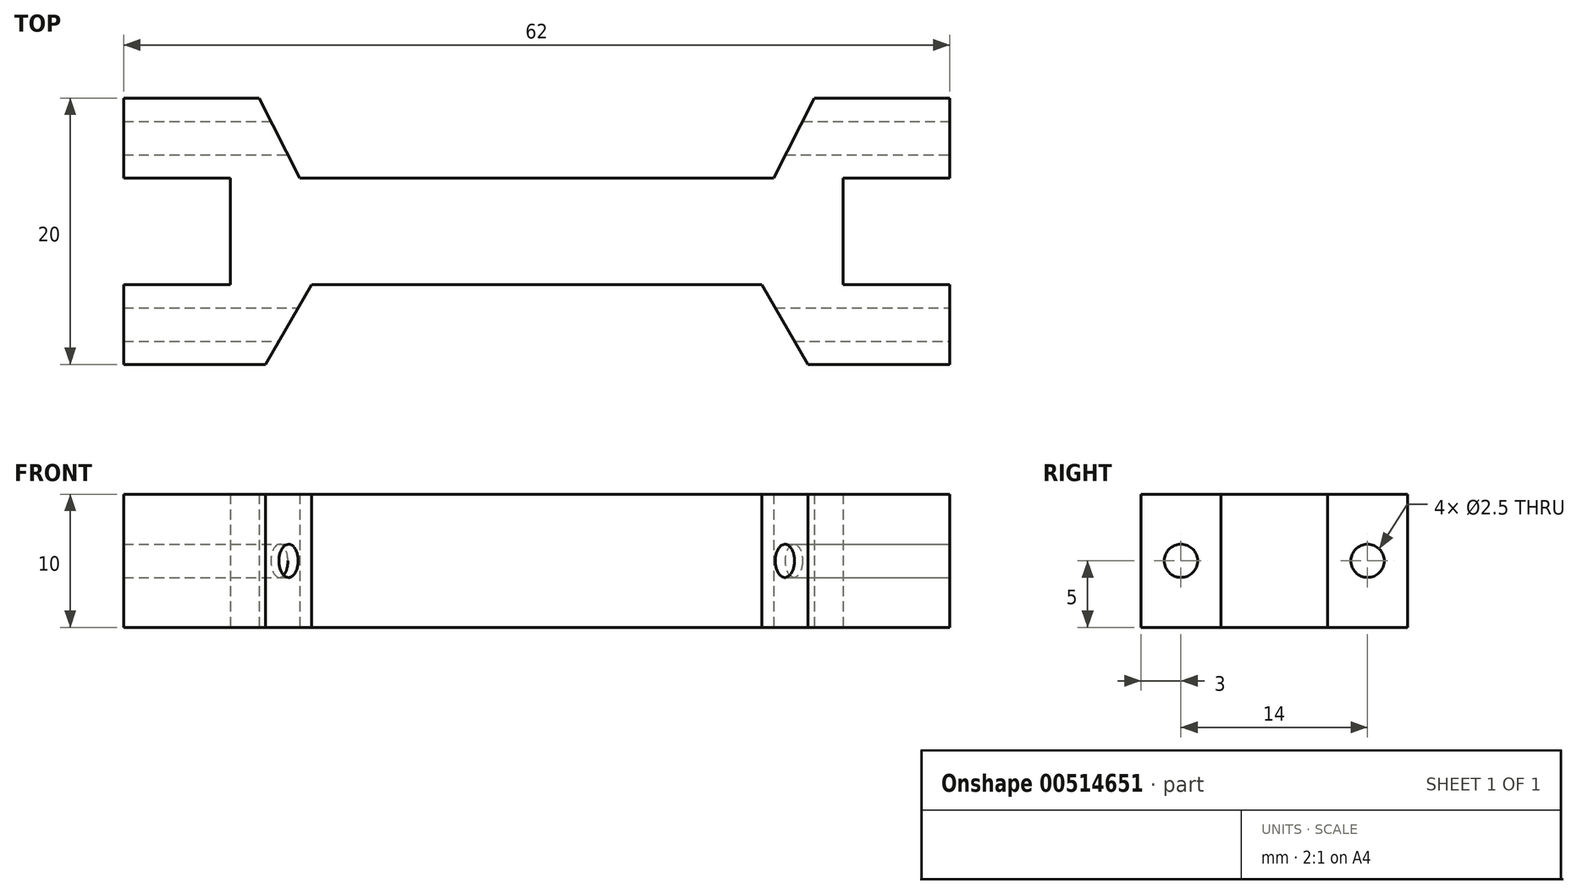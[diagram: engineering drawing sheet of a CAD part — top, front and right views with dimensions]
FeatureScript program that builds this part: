
annotation { "Feature Type Name" : "Feature", "Feature Type Description" : "" }
export const myFeature = defineFeature(function(context is Context, id is Id, definition is map)
    precondition{}
    {
        {
            var Q0;
            Q0=qCreatedBy(makeId("Top.planeOp"),FACE);
            var sketch = newSketch(context, id + "F0", { "sketchPlane" : qUnion([Q0])});
            skLineSegment(sketch, "E0", {"start": v(31, 10) * mm, "end": v(31, 4) * mm});
            skLineSegment(sketch, "E1", {"start": v(31, -10) * mm, "end": v(20.35, -10) * mm});
            skLineSegment(sketch, "E2", {"start": v(31, 4) * mm, "end": v(23, 4) * mm});
            skLineSegment(sketch, "E3", {"start": v(23, 4) * mm, "end": v(23, -4) * mm});
            skLineSegment(sketch, "E4", {"start": v(23, -4) * mm, "end": v(31, -4) * mm});
            skLineSegment(sketch, "E5", {"start": v(17.78, 4) * mm, "end": v(0, 4) * mm});
            skLineSegment(sketch, "E6", {"start": v(16.89, -4) * mm, "end": v(0, -4) * mm});
            skLineSegment(sketch, "E7", {"start": v(17.78, 4) * mm, "end": v(20.84, 10) * mm});
            skLineSegment(sketch, "E8", {"start": v(20.35, -10) * mm, "end": v(16.89, -4) * mm});
            skLineSegment(sketch, "E9.trimOffspring", {"start": v(20.84, 10) * mm, "end": v(31, 10) * mm});
            skPoint(sketch, "E10.orphan", {"position": v(0, 10.31) * mm});
            skLineSegment(sketch, "E11.trimOffspring", {"start": v(31, -4) * mm, "end": v(31, -10) * mm});
            skPoint(sketch, "E12.orphan", {"position": v(23, 14.25) * mm});
            skPoint(sketch, "E13.orphan", {"position": v(23, -14.59) * mm});
            skLineSegment(sketch, "E14.MirrorCS", {"start": v(-17.78, 4) * mm, "end": v(0, 4) * mm});
            skLineSegment(sketch, "E15.MirrorCS", {"start": v(-16.89, -4) * mm, "end": v(0, -4) * mm});
            skLineSegment(sketch, "E16.MirrorCS", {"start": v(-17.78, 4) * mm, "end": v(-20.84, 10) * mm});
            skLineSegment(sketch, "E17.MirrorCS", {"start": v(-20.84, 10) * mm, "end": v(-31, 10) * mm});
            skLineSegment(sketch, "E18.MirrorCS", {"start": v(-31, 10) * mm, "end": v(-31, 4) * mm});
            skLineSegment(sketch, "E19.MirrorCS", {"start": v(-31, 4) * mm, "end": v(-23, 4) * mm});
            skLineSegment(sketch, "E20.MirrorCS", {"start": v(-23, 4) * mm, "end": v(-23, -4) * mm});
            skLineSegment(sketch, "E21.MirrorCS", {"start": v(-23, -4) * mm, "end": v(-31, -4) * mm});
            skLineSegment(sketch, "E22.MirrorCS", {"start": v(-31, -4) * mm, "end": v(-31, -10) * mm});
            skLineSegment(sketch, "E23.MirrorCS", {"start": v(-31, -10) * mm, "end": v(-20.35, -10) * mm});
            skLineSegment(sketch, "E24.MirrorCS", {"start": v(-20.35, -10) * mm, "end": v(-16.89, -4) * mm});
            skSolve(sketch);
        }
        {
            var Q0;
            Q0=makeQuery(id+"F0.imprint","IMPRINT",FACE,{"disambiguationData":[TD([[makeQuery(id+"F0.imprint","IMPRINT",EDGE,{"derivedFrom":sQuery(id+"F0.wireOp",EDGE,"E0")}),-1.0]])]});
            extrude(context, id + "F1", {"entities" : qUnion([Q0]), "depth" : 10 * mm, "offsetDistance" : 25 * mm});
        }
        {
            var Q0;
            Q0=makeQuery(id+"F1.opExtrude","SWEPT_FACE",FACE,{"disambiguationData":[OSD([sQuery(id+"F0.wireOp",EDGE,"E0")])]});
            var sketch = newSketch(context, id + "F2", { "sketchPlane" : qUnion([Q0])});
            skCircle(sketch, "E25", {"center": v(7, 5) * mm, "radius": 1.25 * mm});
            skCircle(sketch, "E26", {"center": v(-7, 5) * mm, "radius": 1.25 * mm});
            skSolve(sketch);
        }
        {
            var Q0;
            Q0=makeQuery(id+"F2.imprint","IMPRINT",FACE,{"disambiguationData":[TD([[makeQuery(id+"F2.imprint","IMPRINT",EDGE,{"derivedFrom":sQuery(id+"F2.wireOp",EDGE,"E26")}),1.0]])]});
            var Q1;
            Q1=makeQuery(id+"F2.imprint","IMPRINT",FACE,{"disambiguationData":[TD([[makeQuery(id+"F2.imprint","IMPRINT",EDGE,{"derivedFrom":sQuery(id+"F2.wireOp",EDGE,"E25")}),1.0]])]});
            extrude(context, id + "F3", {"entities" : qUnion([Q0, Q1]), "operationType" : NewBodyOperationType.REMOVE, "endBound" : BoundingType.THROUGH_ALL, "oppositeDirection" : true, "depth" : 25 * mm, "offsetDistance" : 25 * mm});
        }
    });
